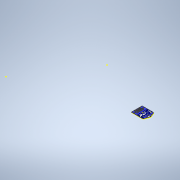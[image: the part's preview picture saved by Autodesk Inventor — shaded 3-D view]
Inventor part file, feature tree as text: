
AUTODESK INVENTOR PART (.ipt)
format: ipt  version: 2020 (Build 240168000, 168)  size: 28,764,672 bytes
history: native  units: mm
features: move_body x18, extrude x14, sketch x10, plane x8, other x7, direct_edit x1, split x1
ambient origin geometry x8: Origin, YZ Plane, XZ Plane, XY Plane, X Axis, Y Axis, Z Axis, Center Point
bodies: Solid1 (feature_tree), Solid2 (feature_tree), Solid3 (feature_tree), Solid4 (feature_tree), Solid5 (feature_tree), Solid6 (feature_tree), Solid7 (feature_tree)
feature tree (59):
  sketch  "Sketch1"  dims[d45=20.0mm d46=0.0mm d48=14.0mm d49=0.0mm]
  extrude  "Extrusion1"  Depth=14.0mm TaperAngle=0.0deg
  extrude  "Extrusion2"  Depth=3.0mm TaperAngle=0.0deg
  extrude  "Extrusion3"  Depth=2.0mm TaperAngle=0.0deg
  extrude  "Extrusion4"  Depth=2.0mm TaperAngle=0.0deg
  plane  "Work Plane1"
  extrude  "Extrusion5"  Depth=2.0mm TaperAngle=0.0deg
  plane  "Work Plane2"
  sketch  "Sketch3"  dims[d62=2.0mm d63=0.0mm d64=2.0mm d65=0.0mm]
  plane  "Work Plane3"
  sketch  "Sketch4"  dims[d66=2.0mm d67=0.0mm d68=2.0mm d69=0.0mm]
  plane  "Work Plane4"
  sketch  "Sketch5"  dims[d70=2.0mm d71=0.0mm d72=2.0mm d73=0.0mm]
  plane  "Work Plane5"
  sketch  "Sketch6"  dims[d74=2.0mm d75=0.0mm d76=20.0mm d77=10.0mm d78=10.0mm]
  plane  "Work Plane6"
  sketch  "Sketch7"  dims[d79=30.0mm d80=10.0mm d81=10.0mm d82=-1710.0mm d83=-76.0mm d84=0.0mm]
  plane  "Work Plane7"
  sketch  "Sketch8"  dims[d85=-33.0mm d86=0.0mm d87=200.0mm d89=90.0deg]
  extrude  "Extrusion6"  Depth=10.0mm
  extrude  "Extrusion7"  TaperAngle=0.0deg  [1 undecoded]
  extrude  "Extrusion8"  TaperAngle=90.0deg  [1 undecoded]
  extrude  "Extrusion9"  [1 undecoded]
  extrude  "Extrusion10"  TaperAngle=180.0deg  [1 undecoded]
  extrude  "Extrusion11"  Depth=3.0mm TaperAngle=0.0deg
  direct_edit  "Direct Edit1"
  move_body  "Move Body5"
  move_body  "Move Body6"
  other  "Logo_UPB"
  other  "MeshFeature2"
  move_body  "Move Body7"
  move_body  "Move Body8"
  move_body  "Move Body9"
  move_body  "Move Body10"
  move_body  "Move Body11"
  move_body  "Move Body12"
  move_body  "Move Body13"
  move_body  "Move Body14"
  move_body  "Move Body15"
  move_body  "Move Body16"
  extrude  "Extrusion12"  Depth=3.0mm TaperAngle=0.0deg
  other  "IMST_lowpoly_3D"
  other  "MeshFeature3"
  move_body  "Move Body17"
  move_body  "Move Body18"
  move_body  "Move Body19"
  move_body  "Move Body20"
  move_body  "Move Body21"
  sketch  "Sketch10"  dims[d94=0.0mm d95=0.0mm d96=-250.0mm d97=180.0deg d98=0.0mm d99=3.0mm d100=0.0mm d101=0.0mm d102=2.0mm d103=0.0mm d104=0.0mm d105=0.0mm d106=-500.0mm d107=0.0mm d108=1.0mm d109=0.0mm d110=10.0mm d111=0.0mm d112=0.0mm d113=80.0mm d115=360.0deg d118=80.0mm d119=360.0deg d120=3.0mm d121=0.0mm d122=90.0deg d123=90.0deg d124=180.0deg d125=200.0mm d126=0.0mm d127=205.0mm d128=2.0mm d129=2.0mm d130=0.0mm d131=3.0mm d132=0.0mm d133=2.0mm d134=0.0mm d135=0.0mm d136=-4.0mm d137=0.0mm d138=3.0mm d139=0.0mm d47=0.5mm]
  extrude  "Extrusion13"  TaperAngle=0.0deg  [1 undecoded]
  extrude  "Extrusion14"  Depth=3.0mm TaperAngle=0.0deg
  plane  "Work Plane8"
  move_body  "Move Body22"
  split  "Split1"
  other  "Image1"
  sketch  "Sketch2"  dims[d50=10.0mm d51=0.0mm d52=3.0mm d53=0.0mm]
  sketch  "Sketch9"  dims[d90=0.0mm d91=3.0mm d92=0.0mm d93=-15.707963mm]
  other  "Scale1"
  other  "Scale2"
note: 5 required parameter values undecoded (feature->parameter linkage not recoverable at this tier; creation-order binding heuristic only, values carry confidence <= 0.55)
